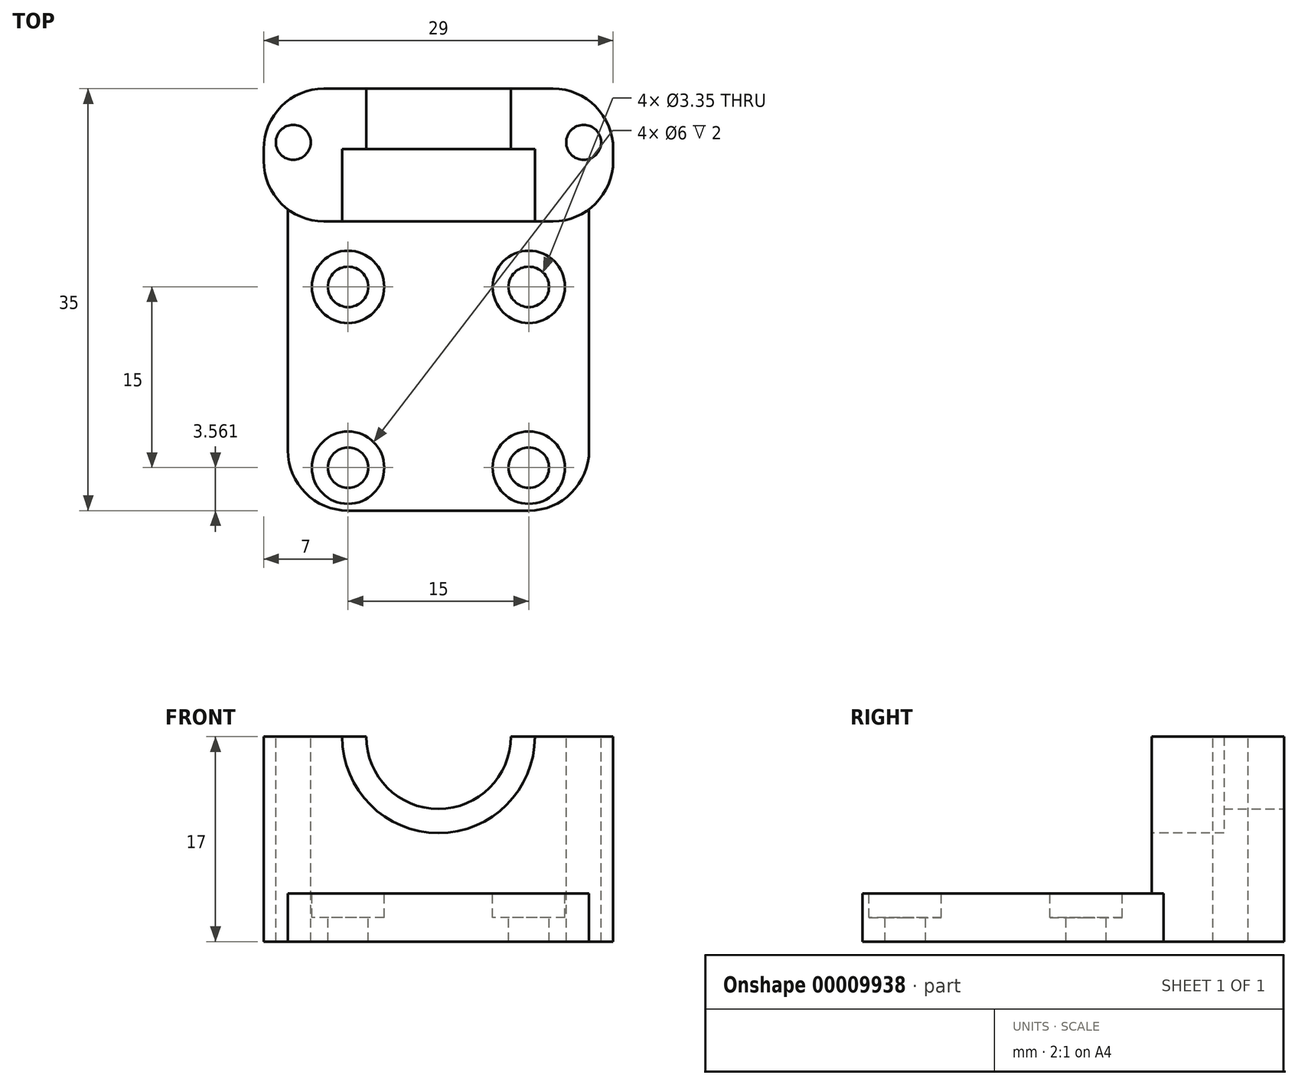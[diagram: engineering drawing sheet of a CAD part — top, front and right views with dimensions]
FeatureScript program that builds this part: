
annotation { "Feature Type Name" : "Feature", "Feature Type Description" : "" }
export const myFeature = defineFeature(function(context is Context, id is Id, definition is map)
    precondition{}
    {
        {
            var Q0;
            Q0=qCreatedBy(makeId("Top.planeOp"),FACE);
            var sketch = newSketch(context, id + "F0", { "sketchPlane" : qUnion([Q0])});
            skLineSegment(sketch, "E0.bottom", {"start": v(0, 0) * mm, "end": v(25, 0) * mm});
            skLineSegment(sketch, "E0.top", {"start": v(0, 35) * mm, "end": v(25, 35) * mm});
            skLineSegment(sketch, "E0.left", {"start": v(0, 0) * mm, "end": v(0, 35) * mm});
            skLineSegment(sketch, "E0.right", {"start": v(25, 0) * mm, "end": v(25, 35) * mm});
            skSolve(sketch);
        }
        {
            var Q0;
            Q0=qSketchRegion(id+"F0",true);
            extrude(context, id + "F1", {"entities" : qUnion([Q0]), "depth" : 4 * mm});
        }
        {
            var Q0;
            Q0=makeQuery(id+"F1.opExtrude","CAP_FACE",FACE,{"disambiguationData":[OSD([sQuery(id+"F0.wireOp",EDGE,"E0.bottom"),sQuery(id+"F0.wireOp",EDGE,"E0.top"),sQuery(id+"F0.wireOp",EDGE,"E0.left"),sQuery(id+"F0.wireOp",EDGE,"E0.right")])],"isStart":false});
            var sketch = newSketch(context, id + "F2", { "sketchPlane" : qUnion([Q0])});
            skCircle(sketch, "E1", {"center": v(5, 18.56) * mm, "radius": 1.68 * mm});
            skCircle(sketch, "E2", {"center": v(20, 18.56) * mm, "radius": 1.68 * mm});
            skCircle(sketch, "E3", {"center": v(5, 3.56) * mm, "radius": 1.68 * mm});
            skCircle(sketch, "E4", {"center": v(20, 3.56) * mm, "radius": 1.68 * mm});
            skLineSegment(sketch, "E5", {"start": v(5, 18.56) * mm, "end": v(0, 18.56) * mm});
            skLineSegment(sketch, "E6", {"start": v(20, 3.56) * mm, "end": v(25, 3.56) * mm});
            skCircle(sketch, "E7", {"center": v(5, 18.56) * mm, "radius": 3 * mm});
            skCircle(sketch, "E8", {"center": v(20, 18.56) * mm, "radius": 3 * mm});
            skCircle(sketch, "E9", {"center": v(5, 3.56) * mm, "radius": 3 * mm});
            skCircle(sketch, "E10", {"center": v(20, 3.56) * mm, "radius": 3 * mm});
            skSolve(sketch);
        }
        {
            var Q0;
            Q0=makeQuery(id+"F2.imprint","IMPRINT",FACE,{"disambiguationData":[TD([[makeQuery(id+"F2.imprint","IMPRINT",EDGE,{"derivedFrom":sQuery(id+"F2.wireOp",EDGE,"E1")}),1.0]])]});
            var Q1;
            Q1=makeQuery(id+"F2.imprint","IMPRINT",FACE,{"disambiguationData":[TD([[makeQuery(id+"F2.imprint","IMPRINT",EDGE,{"derivedFrom":sQuery(id+"F2.wireOp",EDGE,"E2")}),1.0]])]});
            var Q2;
            Q2=makeQuery(id+"F2.imprint","IMPRINT",FACE,{"disambiguationData":[TD([[makeQuery(id+"F2.imprint","IMPRINT",EDGE,{"derivedFrom":sQuery(id+"F2.wireOp",EDGE,"E4")}),1.0]])]});
            var Q3;
            Q3=makeQuery(id+"F2.imprint","IMPRINT",FACE,{"disambiguationData":[TD([[makeQuery(id+"F2.imprint","IMPRINT",EDGE,{"derivedFrom":sQuery(id+"F2.wireOp",EDGE,"E3")}),1.0]])]});
            extrude(context, id + "F3", {"entities" : qUnion([Q0, Q1, Q2, Q3]), "operationType" : NewBodyOperationType.REMOVE, "oppositeDirection" : true, "depth" : 25 * mm});
        }
        {
            var Q0;
            Q0=makeQuery(id+"F1.opExtrude","CAP_FACE",FACE,{"disambiguationData":[OSD([sQuery(id+"F0.wireOp",EDGE,"E0.bottom"),sQuery(id+"F0.wireOp",EDGE,"E0.top"),sQuery(id+"F0.wireOp",EDGE,"E0.left"),sQuery(id+"F0.wireOp",EDGE,"E0.right")])],"isStart":false});
            var sketch = newSketch(context, id + "F4", { "sketchPlane" : qUnion([Q0])});
            skLineSegment(sketch, "E11.bottom", {"start": v(0, 35) * mm, "end": v(25, 35) * mm});
            skLineSegment(sketch, "E11.top", {"start": v(0, 24) * mm, "end": v(25, 24) * mm});
            skLineSegment(sketch, "E11.left", {"start": v(0, 35) * mm, "end": v(0, 24) * mm});
            skLineSegment(sketch, "E11.right", {"start": v(25, 35) * mm, "end": v(25, 24) * mm});
            skSolve(sketch);
        }
        {
            var Q0;
            Q0=qSketchRegion(id+"F4",true);
            extrude(context, id + "F5", {"entities" : qUnion([Q0]), "operationType" : NewBodyOperationType.ADD, "depth" : 13 * mm});
        }
        {
            var Q0;
            Q0=makeQuery(id+"F5.boolean.opBoolean","MERGE",FACE,{"derivedFrom":[makeQuery(id+"F1.opExtrude","SWEPT_FACE",FACE,{"disambiguationData":[OSD([sQuery(id+"F0.wireOp",EDGE,"E0.top")])]}),makeQuery(id+"F5.opExtrude","SWEPT_FACE",FACE,{"disambiguationData":[OSD([sQuery(id+"F4.wireOp",EDGE,"E11.bottom")])]})]});
            var sketch = newSketch(context, id + "F6", { "sketchPlane" : qUnion([Q0])});
            skCircle(sketch, "E12", {"center": v(-12.5, 17) * mm, "radius": 6 * mm});
            skSolve(sketch);
        }
        {
            var Q0;
            {var subQ0=makeQuery(id+"F5.opExtrude","CAP_EDGE",EDGE,{"disambiguationData":[OSD([sQuery(id+"F4.wireOp",EDGE,"E11.bottom")])],"isStart":false});var subQ1=sQuery(id+"F6.wireOp",EDGE,"E12");var subQ3=makeQuery(id+"F6.imprint","INTERSECT",VERTEX,{"disambiguationData":[OD(0.0)],"derivedFrom":[subQ0,subQ1]});Q0=makeQuery(id+"F6.imprint","IMPRINT",FACE,{"disambiguationData":[TD([[makeQuery(id+"F6.imprint","IMPRINT",EDGE,{"disambiguationData":[TD([[subQ3,1.0]])],"derivedFrom":subQ1}),1.0]])]});}
            extrude(context, id + "F7", {"entities" : qUnion([Q0]), "operationType" : NewBodyOperationType.REMOVE, "oppositeDirection" : true, "depth" : 6 * mm});
        }
        {
            var Q0;
            Q0=makeQuery(id+"F5.opExtrude","SWEPT_FACE",FACE,{"disambiguationData":[OSD([sQuery(id+"F4.wireOp",EDGE,"E11.top")])]});
            var sketch = newSketch(context, id + "F8", { "sketchPlane" : qUnion([Q0])});
            skCircle(sketch, "E13", {"center": v(12.5, 17) * mm, "radius": 8 * mm});
            skSolve(sketch);
        }
        {
            var Q0;
            Q0=qSketchRegion(id+"F8",true);
            extrude(context, id + "F9", {"entities" : qUnion([Q0]), "operationType" : NewBodyOperationType.REMOVE, "oppositeDirection" : true, "depth" : 6 * mm});
        }
        {
            var Q0;
            Q0=makeQuery(id+"F2.imprint","IMPRINT",FACE,{"disambiguationData":[TD([[makeQuery(id+"F2.imprint","IMPRINT",EDGE,{"derivedFrom":sQuery(id+"F2.wireOp",EDGE,"E1")}),-1.0]])]});
            var Q1;
            Q1=makeQuery(id+"F2.imprint","IMPRINT",FACE,{"disambiguationData":[TD([[makeQuery(id+"F2.imprint","IMPRINT",EDGE,{"derivedFrom":sQuery(id+"F2.wireOp",EDGE,"E2")}),-1.0]])]});
            var Q2;
            Q2=makeQuery(id+"F2.imprint","IMPRINT",FACE,{"disambiguationData":[TD([[makeQuery(id+"F2.imprint","IMPRINT",EDGE,{"derivedFrom":sQuery(id+"F2.wireOp",EDGE,"E4")}),-1.0]])]});
            var Q3;
            Q3=makeQuery(id+"F2.imprint","IMPRINT",FACE,{"disambiguationData":[TD([[makeQuery(id+"F2.imprint","IMPRINT",EDGE,{"derivedFrom":sQuery(id+"F2.wireOp",EDGE,"E3")}),-1.0]])]});
            extrude(context, id + "F10", {"entities" : qUnion([Q0, Q1, Q2, Q3]), "operationType" : NewBodyOperationType.REMOVE, "oppositeDirection" : true, "depth" : 2 * mm});
        }
        {
            var Q0;
            Q0=makeQuery(id+"F1.opExtrude","SWEPT_EDGE",EDGE,{"disambiguationData":[OSD([sQuery(id+"F0.wireOp",EDGE,"E0.bottom"),sQuery(id+"F0.wireOp",EDGE,"E0.left")])]});
            var Q1;
            Q1=makeQuery(id+"F1.opExtrude","SWEPT_EDGE",EDGE,{"disambiguationData":[OSD([sQuery(id+"F0.wireOp",EDGE,"E0.bottom"),sQuery(id+"F0.wireOp",EDGE,"E0.right")])]});
            fillet(context, id + "F11", {"entities" : qUnion([Q0, Q1]), "radius" : 5 * mm, "tangentPropagation" : true, "allowEdgeOverflow" : false});
        }
        {
            var Q0;
            Q0=makeQuery(id+"F5.boolean.opBoolean","MERGE",FACE,{"derivedFrom":[makeQuery(id+"F1.opExtrude","SWEPT_FACE",FACE,{"disambiguationData":[OSD([sQuery(id+"F0.wireOp",EDGE,"E0.left")])]}),makeQuery(id+"F5.opExtrude","SWEPT_FACE",FACE,{"disambiguationData":[OSD([sQuery(id+"F4.wireOp",EDGE,"E11.left")])]})]});
            var sketch = newSketch(context, id + "F12", { "sketchPlane" : qUnion([Q0])});
            skLineSegment(sketch, "E14.bottom", {"start": v(-35, 0) * mm, "end": v(-24, 0) * mm});
            skLineSegment(sketch, "E14.top", {"start": v(-35, 17) * mm, "end": v(-24, 17) * mm});
            skLineSegment(sketch, "E14.left", {"start": v(-35, 0) * mm, "end": v(-35, 17) * mm});
            skLineSegment(sketch, "E14.right", {"start": v(-24, 0) * mm, "end": v(-24, 17) * mm});
            skSolve(sketch);
        }
        {
            var Q0;
            Q0=qSketchRegion(id+"F12",true);
            extrude(context, id + "F13", {"entities" : qUnion([Q0]), "operationType" : NewBodyOperationType.ADD, "depth" : 2 * mm});
        }
        {
            var Q0;
            Q0=makeQuery(id+"F5.boolean.opBoolean","MERGE",FACE,{"derivedFrom":[makeQuery(id+"F1.opExtrude","SWEPT_FACE",FACE,{"disambiguationData":[OSD([sQuery(id+"F0.wireOp",EDGE,"E0.right")])]}),makeQuery(id+"F5.opExtrude","SWEPT_FACE",FACE,{"disambiguationData":[OSD([sQuery(id+"F4.wireOp",EDGE,"E11.right")])]})]});
            var sketch = newSketch(context, id + "F14", { "sketchPlane" : qUnion([Q0])});
            skLineSegment(sketch, "E15.bottom", {"start": v(35, 0) * mm, "end": v(24, 0) * mm});
            skLineSegment(sketch, "E15.top", {"start": v(35, 17) * mm, "end": v(24, 17) * mm});
            skLineSegment(sketch, "E15.left", {"start": v(35, 0) * mm, "end": v(35, 17) * mm});
            skLineSegment(sketch, "E15.right", {"start": v(24, 0) * mm, "end": v(24, 17) * mm});
            skSolve(sketch);
        }
        {
            var Q0;
            Q0=qSketchRegion(id+"F14",true);
            extrude(context, id + "F15", {"entities" : qUnion([Q0]), "operationType" : NewBodyOperationType.ADD, "depth" : 2 * mm});
        }
        {
            var Q0;
            {var subQ0=sQuery(id+"F4.wireOp",EDGE,"E11.bottom");var subQ1=sQuery(id+"F4.wireOp",EDGE,"E11.top");var subQ2=sQuery(id+"F4.wireOp",EDGE,"E11.left");Q0=makeQuery(id+"F9.boolean.opBoolean","SPLIT",FACE,{"disambiguationData":[TD([makeQuery(id+"F1.opExtrude","SWEPT_FACE",FACE,{"disambiguationData":[OSD([sQuery(id+"F0.wireOp",EDGE,"E0.left")])]})])],"derivedFrom":makeQuery(id+"F5.opExtrude","CAP_FACE",FACE,{"disambiguationData":[OSD([subQ0,subQ1,subQ2,sQuery(id+"F4.wireOp",EDGE,"E11.right")])],"isStart":false})});}
            var sketch = newSketch(context, id + "F16", { "sketchPlane" : qUnion([Q0])});
            skCircle(sketch, "E16", {"center": v(0.45, 30.55) * mm, "radius": 1.45 * mm});
            skCircle(sketch, "E17", {"center": v(24.55, 30.55) * mm, "radius": 1.45 * mm});
            skSolve(sketch);
        }
        {
            var Q0;
            Q0=qSketchRegion(id+"F16",true);
            extrude(context, id + "F17", {"entities" : qUnion([Q0]), "operationType" : NewBodyOperationType.REMOVE, "oppositeDirection" : true, "depth" : 25 * mm});
        }
        {
            var Q0;
            Q0=makeQuery(id+"F13.opExtrude","CAP_EDGE",EDGE,{"disambiguationData":[OSD([sQuery(id+"F12.wireOp",EDGE,"E14.right")])],"isStart":false});
            var Q1;
            Q1=makeQuery(id+"F13.opExtrude","CAP_EDGE",EDGE,{"disambiguationData":[OSD([sQuery(id+"F12.wireOp",EDGE,"E14.left")])],"isStart":false});
            var Q2;
            Q2=makeQuery(id+"F15.opExtrude","CAP_EDGE",EDGE,{"disambiguationData":[OSD([sQuery(id+"F14.wireOp",EDGE,"E15.left")])],"isStart":false});
            var Q3;
            Q3=makeQuery(id+"F15.opExtrude","CAP_EDGE",EDGE,{"disambiguationData":[OSD([sQuery(id+"F14.wireOp",EDGE,"E15.right")])],"isStart":false});
            fillet(context, id + "F18", {"entities" : qUnion([Q0, Q1, Q2, Q3]), "radius" : 5 * mm, "tangentPropagation" : true, "allowEdgeOverflow" : false});
        }
    });
